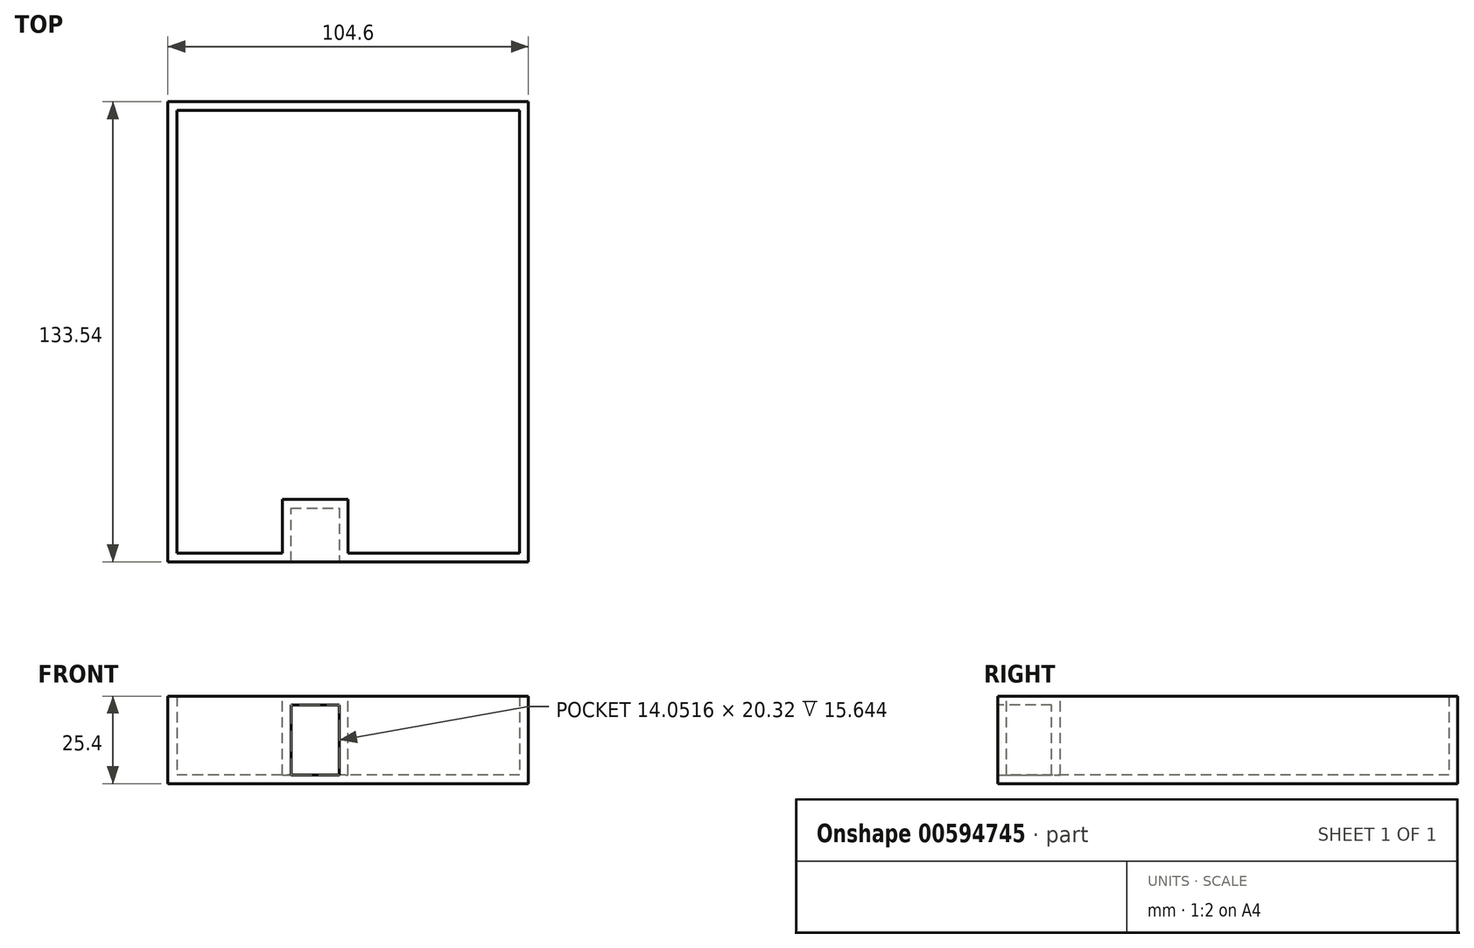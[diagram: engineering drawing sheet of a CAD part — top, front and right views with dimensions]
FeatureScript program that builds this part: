
annotation { "Feature Type Name" : "Feature", "Feature Type Description" : "" }
export const myFeature = defineFeature(function(context is Context, id is Id, definition is map)
    precondition{}
    {
        {
            var Q0;
            Q0=qCreatedBy(makeId("Top.planeOp"),FACE);
            var sketch = newSketch(context, id + "F0", { "sketchPlane" : qUnion([Q0])});
            skLineSegment(sketch, "E0.bottom", {"start": v(52.3, 57.56) * mm, "end": v(-52.3, 57.56) * mm});
            skLineSegment(sketch, "E0.top", {"start": v(52.3, -75.98) * mm, "end": v(-52.3, -75.98) * mm});
            skLineSegment(sketch, "E0.left", {"start": v(52.3, 57.56) * mm, "end": v(52.3, -75.98) * mm});
            skLineSegment(sketch, "E0.right", {"start": v(-52.3, 57.56) * mm, "end": v(-52.3, -75.98) * mm});
            skPoint(sketch, "E0.middle", {"position": v(0, -9.21) * mm});
            skSolve(sketch);
        }
        {
            var Q0;
            Q0=makeQuery(id+"F0.imprint","IMPRINT",FACE,{"disambiguationData":[TD([[makeQuery(id+"F0.imprint","IMPRINT",EDGE,{"derivedFrom":sQuery(id+"F0.wireOp",EDGE,"E0.bottom")}),1.0]])]});
            extrude(context, id + "F1", {"entities" : qUnion([Q0]), "depth" : 25.4 * mm, "offsetDistance" : 25.4 * mm});
        }
        {
            var Q0;
            Q0=makeQuery(id+"F1.opExtrude","CAP_FACE",FACE,{"disambiguationData":[OSD([sQuery(id+"F0.wireOp",EDGE,"E0.bottom"),sQuery(id+"F0.wireOp",EDGE,"E0.top"),sQuery(id+"F0.wireOp",EDGE,"E0.left"),sQuery(id+"F0.wireOp",EDGE,"E0.right")])],"isStart":false});
            shell(context, id + "F2", {"entities" : qUnion([Q0]), "thickness" : 2.54 * mm});
        }
        {
            var Q0;
            Q0=makeQuery(id+"F1.opExtrude","SWEPT_FACE",FACE,{"disambiguationData":[OSD([sQuery(id+"F0.wireOp",EDGE,"E0.top")])]});
            var sketch = newSketch(context, id + "F3", { "sketchPlane" : qUnion([Q0])});
            skLineSegment(sketch, "E1.bottom", {"start": v(0, 0) * mm, "end": v(-19.13, 0) * mm});
            skLineSegment(sketch, "E1.top", {"start": v(0, 25.4) * mm, "end": v(-19.13, 25.4) * mm});
            skLineSegment(sketch, "E1.left", {"start": v(0, 0) * mm, "end": v(0, 25.4) * mm});
            skLineSegment(sketch, "E1.right", {"start": v(-19.13, 0) * mm, "end": v(-19.13, 25.4) * mm});
            skSolve(sketch);
        }
        {
            var Q0;
            Q0=makeQuery(id+"F3.imprint","IMPRINT",FACE,{"disambiguationData":[TD([[makeQuery(id+"F3.imprint","IMPRINT",EDGE,{"derivedFrom":sQuery(id+"F3.wireOp",EDGE,"E1.bottom")}),-1.0]])]});
            extrude(context, id + "F4", {"entities" : qUnion([Q0]), "operationType" : NewBodyOperationType.ADD, "oppositeDirection" : true, "depth" : 18.18 * mm, "offsetDistance" : 25.4 * mm});
        }
        {
            var Q0;
            Q0=makeQuery(id+"F1.opExtrude","SWEPT_FACE",FACE,{"disambiguationData":[OSD([sQuery(id+"F0.wireOp",EDGE,"E0.top")])]});
            shell(context, id + "F5", {"entities" : qUnion([Q0]), "thickness" : 2.54 * mm});
        }
    });
